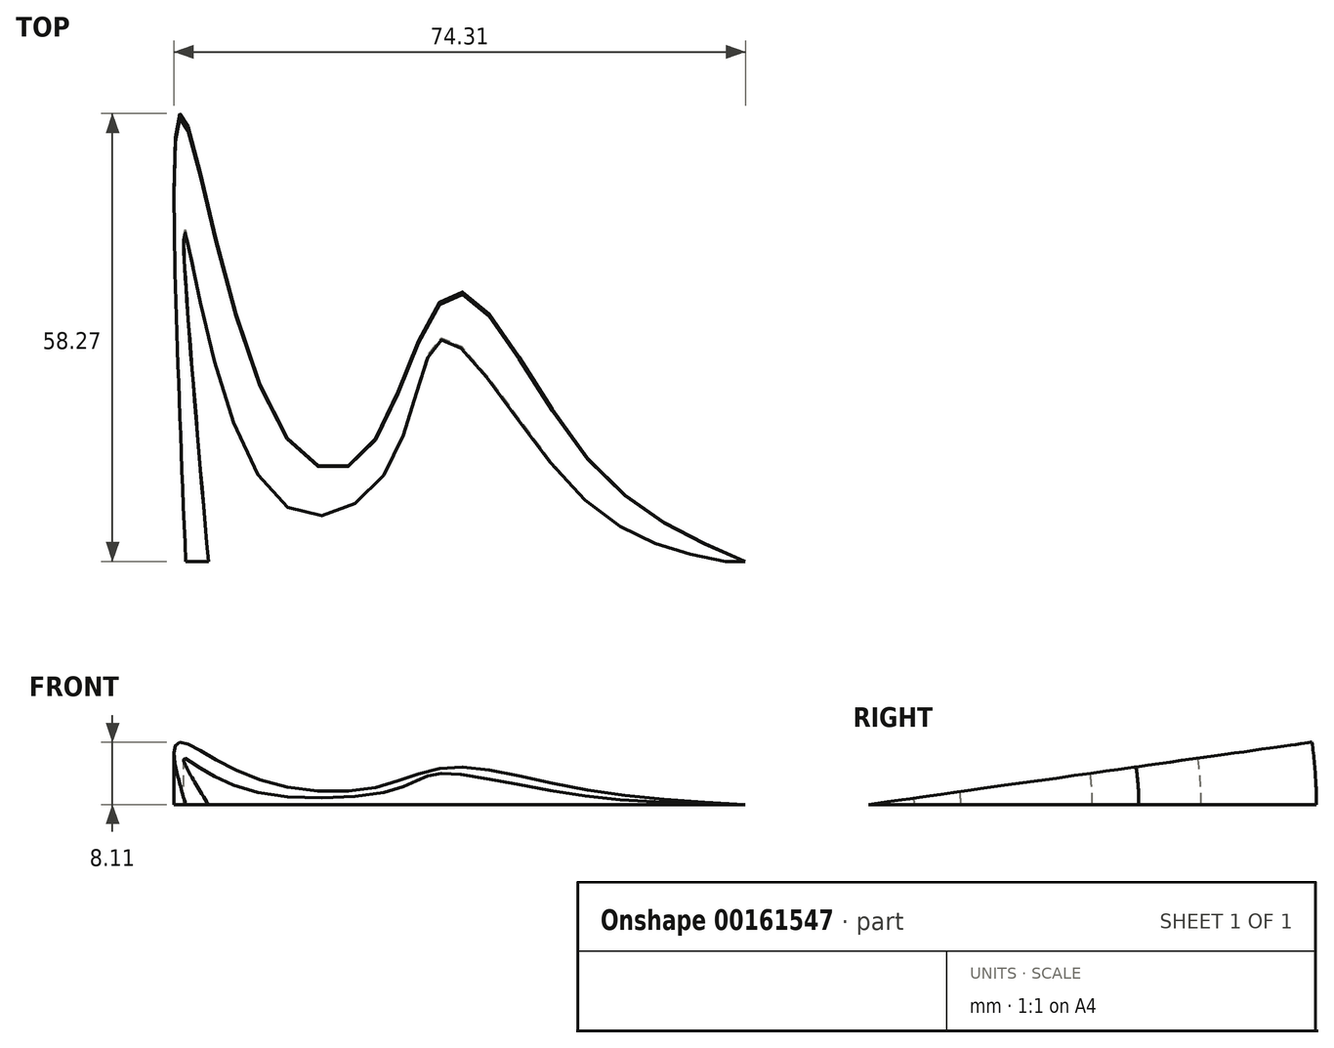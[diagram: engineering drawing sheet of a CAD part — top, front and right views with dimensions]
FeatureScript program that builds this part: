
annotation { "Feature Type Name" : "Feature", "Feature Type Description" : "" }
export const myFeature = defineFeature(function(context is Context, id is Id, definition is map)
    precondition{}
    {
        {
            var Q0;
            Q0=qCreatedBy(makeId("Top.planeOp"),FACE);
            var sketch = newSketch(context, id + "F0", { "sketchPlane" : qUnion([Q0])});
            skFitSpline(sketch, "E0", {"points": [v(-64.27, 0) * mm, v(-64.6, 58.04) * mm, v(-51.48, 16.72) * mm, v(-40.99, 14.1) * mm, v(-29.51, 35.09) * mm, v(-12.79, 14.43) * mm, v(8.53, 0) * mm], "startDerivative": vector(-16.09, 393.33) * mm, "endDerivative": vector(142.44, -59.97) * mm});
            skLineSegment(sketch, "E1", {"start": v(-64.27, 0) * mm, "end": v(8.53, 0) * mm});
            skSolve(sketch);
        }
        {
            var Q0;
            Q0=makeQuery(id+"F0.imprint","IMPRINT",FACE,{"disambiguationData":[TD([[makeQuery(id+"F0.imprint","IMPRINT",EDGE,{"derivedFrom":sQuery(id+"F0.wireOp",EDGE,"E0")}),-1.0]])]});
            var Q1;
            Q1=sQuery(id+"F0.wireOp",EDGE,"E1");
            revolve(context, id + "F1", {"entities" : qUnion([Q0]), "axis" : qUnion([Q1]), "revolveType" : RevolveType.ONE_DIRECTION, "angle" : 8 * degree});
        }
        {
            var Q0;
            Q0=makeQuery(id+"F1.opRevolve","CAP_FACE",FACE,{"disambiguationData":[OSD([sQuery(id+"F0.wireOp",EDGE,"E0"),sQuery(id+"F0.wireOp",EDGE,"E1")])],"isStart":false});
            var sketch = newSketch(context, id + "F2", { "sketchPlane" : qUnion([Q0])});
            skFitSpline(sketch, "E2", {"points": [v(-61.32, 0) * mm, v(-64.27, 43.02) * mm, v(-52.52, 8.31) * mm, v(-38, 12.15) * mm, v(-30.84, 29.12) * mm, v(-13.16, 8.86) * mm, v(5.96, 0) * mm], "startDerivative": vector(-27.6, 321.13) * mm, "endDerivative": vector(127.77, -25.19) * mm});
            skLineSegment(sketch, "E3", {"start": v(-61.32, 0) * mm, "end": v(5.96, 0) * mm});
            skSolve(sketch);
        }
        {
            var Q0;
            Q0 = qSketchRegion(id + "F2", true);
            var Q1;
            Q1=sQuery(id+"F2.wireOp",EDGE,"E3");
            revolve(context, id + "F3", {"operationType" : NewBodyOperationType.REMOVE, "entities" : qUnion([Q0]), "axis" : qUnion([Q1]), "revolveType" : RevolveType.FULL, "oppositeDirection" : true});
        }
    });
